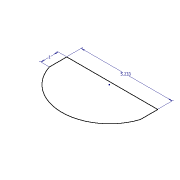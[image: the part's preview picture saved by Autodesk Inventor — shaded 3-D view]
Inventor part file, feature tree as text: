
AUTODESK INVENTOR PART (.ipt)
format: ipt  version: 2015 (Build 190159000, 159)  size: 58,880 bytes
history: native  units: mm
features: sketch x1
ambient origin geometry x8: Origin, YZ Plane, XZ Plane, XY Plane, X Axis, Y Axis, Z Axis, Center Point
feature tree (1):
  sketch  "Sketch1"  dims[d2=1.0mm d3=5.232625mm]
